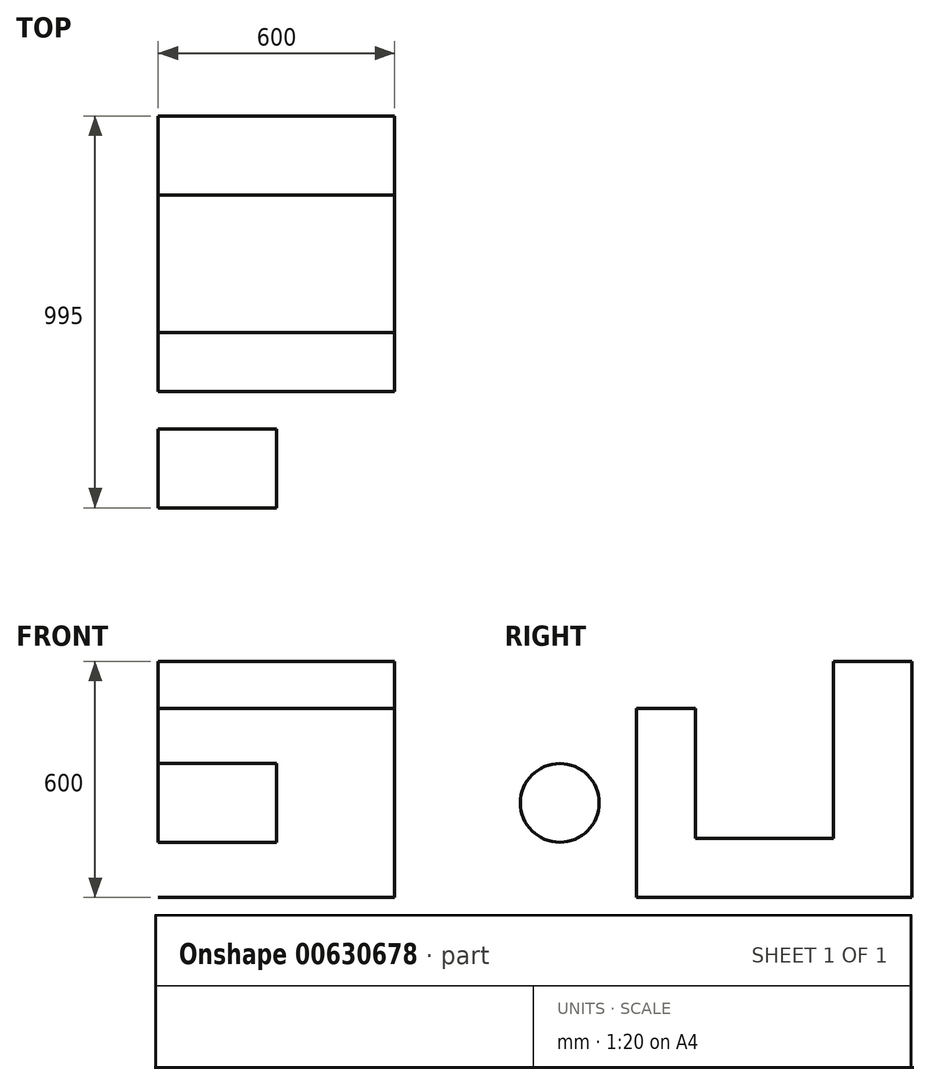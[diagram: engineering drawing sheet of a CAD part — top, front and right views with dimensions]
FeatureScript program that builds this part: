
annotation { "Feature Type Name" : "Feature", "Feature Type Description" : "" }
export const myFeature = defineFeature(function(context is Context, id is Id, definition is map)
    precondition{}
    {
        {
            var Q0;
            Q0=qCreatedBy(makeId("Right.planeOp"),FACE);
            var sketch = newSketch(context, id + "F0", { "sketchPlane" : qUnion([Q0])});
            skLineSegment(sketch, "E0.bottom", {"start": v(350, -300) * mm, "end": v(-350, -300) * mm});
            skLineSegment(sketch, "E0.top", {"start": v(350, 300) * mm, "end": v(-350, 300) * mm});
            skLineSegment(sketch, "E0.left", {"start": v(350, -300) * mm, "end": v(350, 300) * mm});
            skLineSegment(sketch, "E0.right", {"start": v(-350, -300) * mm, "end": v(-350, 300) * mm});
            skPoint(sketch, "E0.middle", {"position": v(0, 0) * mm});
            skSolve(sketch);
        }
        {
            var Q0;
            Q0=makeQuery(id+"F0.imprint","IMPRINT",FACE,{"disambiguationData":[TD([[makeQuery(id+"F0.imprint","IMPRINT",EDGE,{"derivedFrom":sQuery(id+"F0.wireOp",EDGE,"E0.bottom")}),-1.0]])]});
            extrude(context, id + "F1", {"entities" : qUnion([Q0]), "depth" : 600 * mm, "offsetDistance" : 25 * mm});
        }
        {
            var Q0;
            Q0=makeQuery(id+"F1.opExtrude","CAP_FACE",FACE,{"disambiguationData":[OSD([sQuery(id+"F0.wireOp",EDGE,"E0.bottom"),sQuery(id+"F0.wireOp",EDGE,"E0.top"),sQuery(id+"F0.wireOp",EDGE,"E0.left"),sQuery(id+"F0.wireOp",EDGE,"E0.right")])],"isStart":false});
            var sketch = newSketch(context, id + "F2", { "sketchPlane" : qUnion([Q0])});
            skLineSegment(sketch, "E1", {"start": v(350, 300) * mm, "end": v(150, 300) * mm});
            skLineSegment(sketch, "E2", {"start": v(150, 300) * mm, "end": v(-200, 300) * mm});
            skLineSegment(sketch, "E3", {"start": v(-200, 300) * mm, "end": v(-350, 300) * mm});
            skPoint(sketch, "E4.endSnap0", {"position": v(0, -300) * mm});
            skLineSegment(sketch, "E5", {"start": v(0, -150) * mm, "end": v(-350, -150) * mm});
            skLineSegment(sketch, "E6", {"start": v(-350, -150) * mm, "end": v(350, -150) * mm});
            skLineSegment(sketch, "E7", {"start": v(-200, 300) * mm, "end": v(-200, -150) * mm});
            skLineSegment(sketch, "E8", {"start": v(150, 300) * mm, "end": v(150, -150) * mm});
            skSolve(sketch);
        }
        {
            var Q0;
            Q0=makeQuery(id+"F2.imprint","IMPRINT",FACE,{"disambiguationData":[TD([[makeQuery(id+"F2.imprint","IMPRINT",EDGE,{"derivedFrom":sQuery(id+"F2.wireOp",EDGE,"E2")}),1.0]])]});
            extrude(context, id + "F3", {"entities" : qUnion([Q0]), "operationType" : NewBodyOperationType.REMOVE, "endBound" : BoundingType.THROUGH_ALL, "oppositeDirection" : true, "depth" : 25 * mm, "offsetDistance" : 25 * mm});
        }
        {
            var Q0;
            Q0=makeQuery(id+"F1.opExtrude","CAP_FACE",FACE,{"disambiguationData":[OSD([sQuery(id+"F0.wireOp",EDGE,"E0.bottom"),sQuery(id+"F0.wireOp",EDGE,"E0.top"),sQuery(id+"F0.wireOp",EDGE,"E0.left"),sQuery(id+"F0.wireOp",EDGE,"E0.right")])],"isStart":false});
            var sketch = newSketch(context, id + "F4", { "sketchPlane" : qUnion([Q0])});
            skLineSegment(sketch, "E9", {"start": v(-350, 300) * mm, "end": v(-350, 180) * mm});
            skLineSegment(sketch, "E10", {"start": v(-200, 180) * mm, "end": v(-350, 180) * mm});
            skSolve(sketch);
        }
        {
            var Q0;
            Q0 = qSketchRegion(id + "F4", true);
            var Q1;
            Q1=makeQuery(id+"F4.imprint","IMPRINT",FACE,{"disambiguationData":[TD([[makeQuery(id+"F4.imprint","IMPRINT",EDGE,{"derivedFrom":sQuery(id+"F4.wireOp",EDGE,"E9")}),-1.0]])]});
            extrude(context, id + "F5", {"entities" : qUnion([Q0, Q1]), "operationType" : NewBodyOperationType.REMOVE, "endBound" : BoundingType.THROUGH_ALL, "oppositeDirection" : true, "depth" : 25 * mm, "offsetDistance" : 25 * mm});
        }
        {
            var Q0;
            Q0=makeQuery(id+"F1.opExtrude","SWEPT_FACE",FACE,{"disambiguationData":[OSD([sQuery(id+"F0.wireOp",EDGE,"E0.right")])]});
            var sketch = newSketch(context, id + "F6", { "sketchPlane" : qUnion([Q0])});
            skLineSegment(sketch, "E11", {"start": v(300, 180) * mm, "end": v(300, -300) * mm});
            skSolve(sketch);
        }
        {
            var Q0;
            {var subQ0=sQuery(id+"F6.wireOp",EDGE,"E11");Q0=makeQuery(id+"F6.imprint","IMPRINT",FACE,{"disambiguationData":[TD([[makeQuery(id+"F6.imprint","IMPRINT",EDGE,{"derivedFrom":subQ0}),-1.0]])]});}
            extrude(context, id + "F7", {"entities" : qUnion([Q0]), "operationType" : NewBodyOperationType.ADD, "depth" : 195 * mm, "offsetDistance" : 25 * mm});
        }
        {
            var Q0;
            {var subQ0=sQuery(id+"F0.wireOp",EDGE,"E0.right");Q0=makeQuery(id+"F7.boolean.opBoolean","MERGE",FACE,{"derivedFrom":[makeQuery(id+"F1.opExtrude","CAP_FACE",FACE,{"disambiguationData":[OSD([sQuery(id+"F0.wireOp",EDGE,"E0.bottom"),sQuery(id+"F0.wireOp",EDGE,"E0.top"),sQuery(id+"F0.wireOp",EDGE,"E0.left"),subQ0])],"isStart":true}),makeQuery(id+"F7.opExtrude","SWEPT_FACE",FACE,{"disambiguationData":[OSD([subQ0])]})]});}
            var sketch = newSketch(context, id + "F8", { "sketchPlane" : qUnion([Q0])});
            skCircle(sketch, "E12", {"center": v(545, -60) * mm, "radius": 240 * mm});
            skSolve(sketch);
        }
        {
            var Q0;
            {var subQ1=sQuery(id+"F0.wireOp",EDGE,"E0.right");var subQ3=makeQuery(id+"F7.opExtrude","CAP_EDGE",EDGE,{"disambiguationData":[OSD([subQ1])],"isStart":false});Q0=makeQuery(id+"F8.imprint","IMPRINT",FACE,{"disambiguationData":[TD([[makeQuery(id+"F8.imprint","IMPRINT",EDGE,{"derivedFrom":subQ3}),-1.0]])]});}
            extrude(context, id + "F9", {"entities" : qUnion([Q0]), "operationType" : NewBodyOperationType.ADD, "oppositeDirection" : true, "depth" : 300 * mm, "offsetDistance" : 25 * mm});
        }
        {
            var Q0;
            Q0=makeQuery(id+"F9.boolean.opBoolean","MERGE",FACE,{"derivedFrom":[makeQuery(id+"F7.opExtrude","SWEPT_FACE",FACE,{"disambiguationData":[OSD([sQuery(id+"F6.wireOp",EDGE,"E11")])]}),makeQuery(id+"F9.opExtrude","CAP_FACE",FACE,{"disambiguationData":[OSD([sQuery(id+"F0.wireOp",EDGE,"E0.right"),sQuery(id+"F8.wireOp",EDGE,"E12")])],"isStart":false})]});
            var sketch = newSketch(context, id + "F10", { "sketchPlane" : qUnion([Q0])});
            skLineSegment(sketch, "E13", {"start": v(-545, 180) * mm, "end": v(-545, -300) * mm});
            skCircle(sketch, "E14", {"center": v(-545, -60) * mm, "radius": 100 * mm});
            skSolve(sketch);
        }
        {
            var Q0;
            {var subQ0=sQuery(id+"F10.wireOp",EDGE,"E14");var subQ1=sQuery(id+"F10.wireOp",EDGE,"E13");var subQ2=makeQuery(id+"F10.imprint","INTERSECT",VERTEX,{"disambiguationData":[OD(0.0)],"derivedFrom":[subQ1,subQ0]});Q0=makeQuery(id+"F10.imprint","IMPRINT",FACE,{"disambiguationData":[TD([[makeQuery(id+"F10.imprint","IMPRINT",EDGE,{"disambiguationData":[TD([[subQ2,-1.0]])],"derivedFrom":subQ1}),1.0]])]});}
            var Q1;
            {var subQ0=sQuery(id+"F10.wireOp",EDGE,"E14");var subQ1=sQuery(id+"F10.wireOp",EDGE,"E13");var subQ2=makeQuery(id+"F10.imprint","INTERSECT",VERTEX,{"disambiguationData":[OD(0.0)],"derivedFrom":[subQ1,subQ0]});Q1=makeQuery(id+"F10.imprint","IMPRINT",FACE,{"disambiguationData":[TD([[makeQuery(id+"F10.imprint","IMPRINT",EDGE,{"disambiguationData":[TD([[subQ2,-1.0]])],"derivedFrom":subQ1}),-1.0]])]});}
            extrude(context, id + "F11", {"entities" : qUnion([Q0, Q1]), "operationType" : NewBodyOperationType.REMOVE, "endBound" : BoundingType.THROUGH_ALL, "oppositeDirection" : true, "depth" : 25 * mm, "offsetDistance" : 25 * mm});
        }
    });
